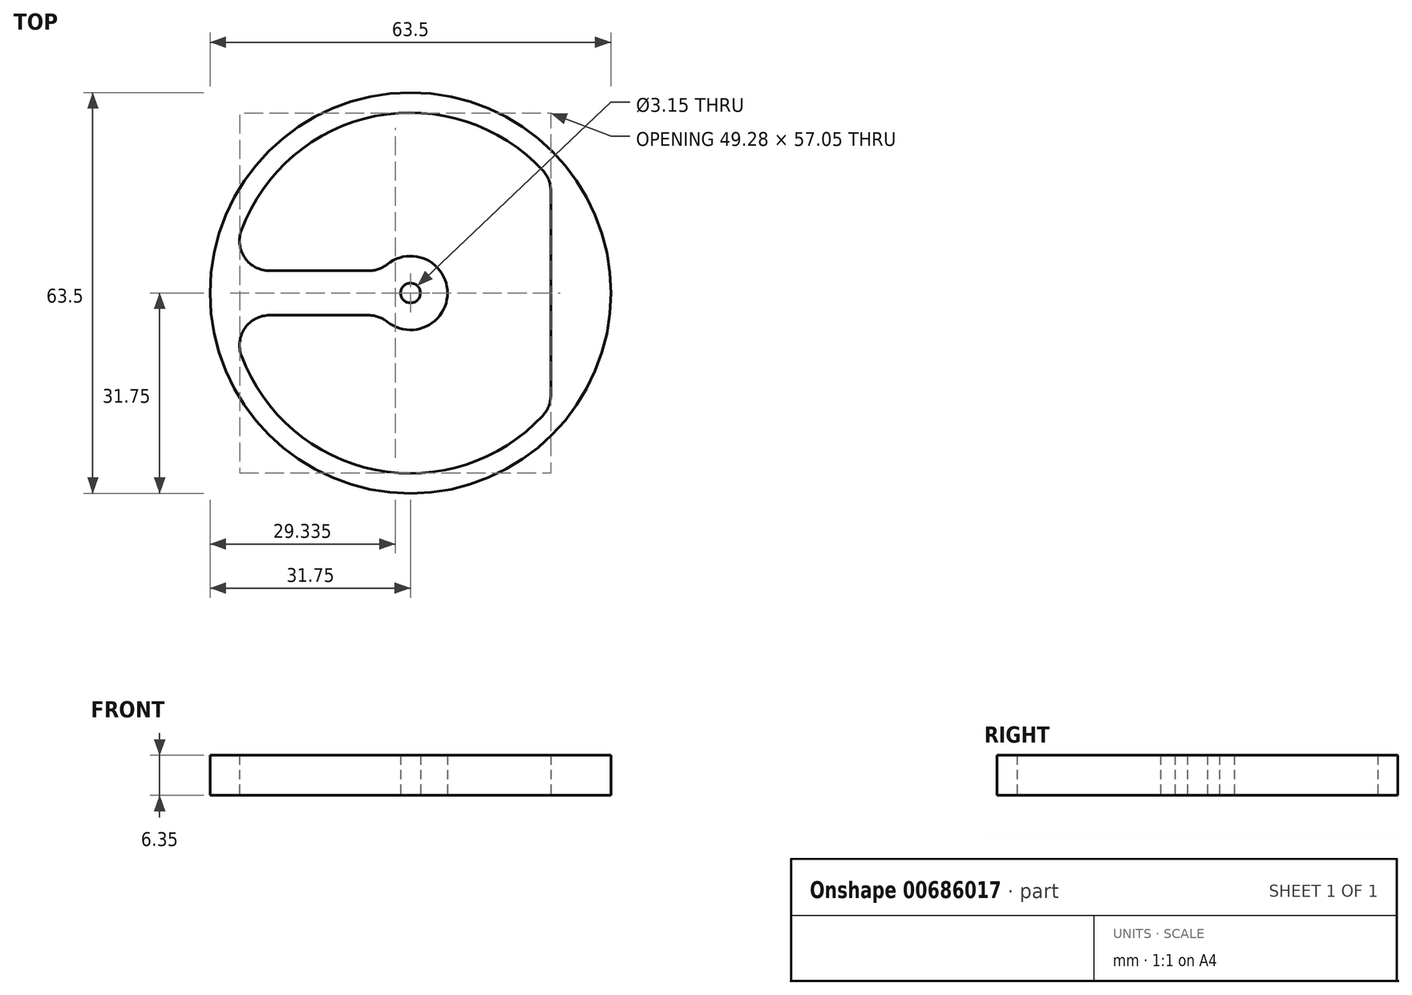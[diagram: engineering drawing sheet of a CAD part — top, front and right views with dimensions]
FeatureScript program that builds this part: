
annotation { "Feature Type Name" : "Feature", "Feature Type Description" : "" }
export const myFeature = defineFeature(function(context is Context, id is Id, definition is map)
    precondition{}
    {
        {
            var Q0;
            Q0=qCreatedBy(makeId("Top.planeOp"),FACE);
            var sketch = newSketch(context, id + "F0", { "sketchPlane" : qUnion([Q0])});
            skCircle(sketch, "E0", {"center": v(0, 0) * mm, "radius": 31.75 * mm});
            skArc(sketch, "E1", {"start": v(-26.79, -9.94) * mm, "mid": v(-5.57, -28.03) * mm, "end": v(20.96, -19.43) * mm});
            skCircle(sketch, "E2", {"center": v(0, 0) * mm, "radius": 1.57 * mm});
            skArc(sketch, "E3", {"start": v(-3.66, -4.57) * mm, "mid": v(5.85, 0) * mm, "end": v(-3.66, 4.57) * mm});
            skLineSegment(sketch, "E4.bottom", {"start": v(-6.64, 3.52) * mm, "end": v(-22.32, 3.52) * mm});
            skLineSegment(sketch, "E4.top", {"start": v(-6.64, -3.52) * mm, "end": v(-22.32, -3.52) * mm});
            skLineSegment(sketch, "E5", {"start": v(22.22, 0) * mm, "end": v(22.22, -16.19) * mm});
            skLineSegment(sketch, "E6", {"start": v(22.22, 0) * mm, "end": v(22.22, 16.19) * mm});
            skPoint(sketch, "E7.end.orphan", {"position": v(-5.85, 0) * mm});
            skArc(sketch, "E8.trimOffspring", {"start": v(20.95, 19.43) * mm, "mid": v(-5.57, 28.03) * mm, "end": v(-26.79, 9.94) * mm});
            skArc(sketch, "E9.filletArc", {"start": v(-26.79, 9.94) * mm, "mid": v(-26.23, 5.57) * mm, "end": v(-22.32, 3.52) * mm});
            skArc(sketch, "E10.filletArc", {"start": v(-22.32, -3.52) * mm, "mid": v(-26.23, -5.57) * mm, "end": v(-26.79, -9.94) * mm});
            skArc(sketch, "E11.filletArc", {"start": v(20.96, -19.43) * mm, "mid": v(21.9, -17.93) * mm, "end": v(22.23, -16.19) * mm});
            skArc(sketch, "E12.filletArc", {"start": v(22.22, 16.19) * mm, "mid": v(21.9, 17.93) * mm, "end": v(20.95, 19.43) * mm});
            skArc(sketch, "E13.filletArc", {"start": v(-6.64, 3.52) * mm, "mid": v(-5.06, 3.8) * mm, "end": v(-3.66, 4.57) * mm});
            skArc(sketch, "E14.filletArc", {"start": v(-3.66, -4.57) * mm, "mid": v(-5.06, -3.8) * mm, "end": v(-6.64, -3.52) * mm});
            skLineSegment(sketch, "E15.0", {"start": v(-6.64, -8.29) * mm, "end": v(-22.32, -8.29) * mm});
            skArc(sketch, "E15.1", {"start": v(-6.64, -8.29) * mm, "mid": v(10.62, 0) * mm, "end": v(-6.64, 8.29) * mm});
            skLineSegment(sketch, "E15.2", {"start": v(17.46, 0) * mm, "end": v(17.46, -16.19) * mm});
            skLineSegment(sketch, "E15.3", {"start": v(17.46, 0) * mm, "end": v(17.46, 16.19) * mm});
            skArc(sketch, "E15.4", {"start": v(17.46, 16.19) * mm, "mid": v(-4.64, 23.36) * mm, "end": v(-22.32, 8.29) * mm});
            skArc(sketch, "E15.5", {"start": v(-22.32, -8.29) * mm, "mid": v(-4.64, -23.36) * mm, "end": v(17.46, -16.19) * mm});
            skLineSegment(sketch, "E15.6", {"start": v(-6.64, 8.29) * mm, "end": v(-22.32, 8.29) * mm});
            skSolve(sketch);
        }
        {
            var Q0;
            Q0=makeQuery(id+"F0.imprint","IMPRINT",FACE,{"disambiguationData":[TD([[makeQuery(id+"F0.imprint","IMPRINT",EDGE,{"derivedFrom":sQuery(id+"F0.wireOp",EDGE,"E0")}),1.0]])]});
            extrude(context, id + "F1", {"entities" : qUnion([Q0]), "depth" : 6.35 * mm, "offsetDistance" : 25.4 * mm});
        }
    });
